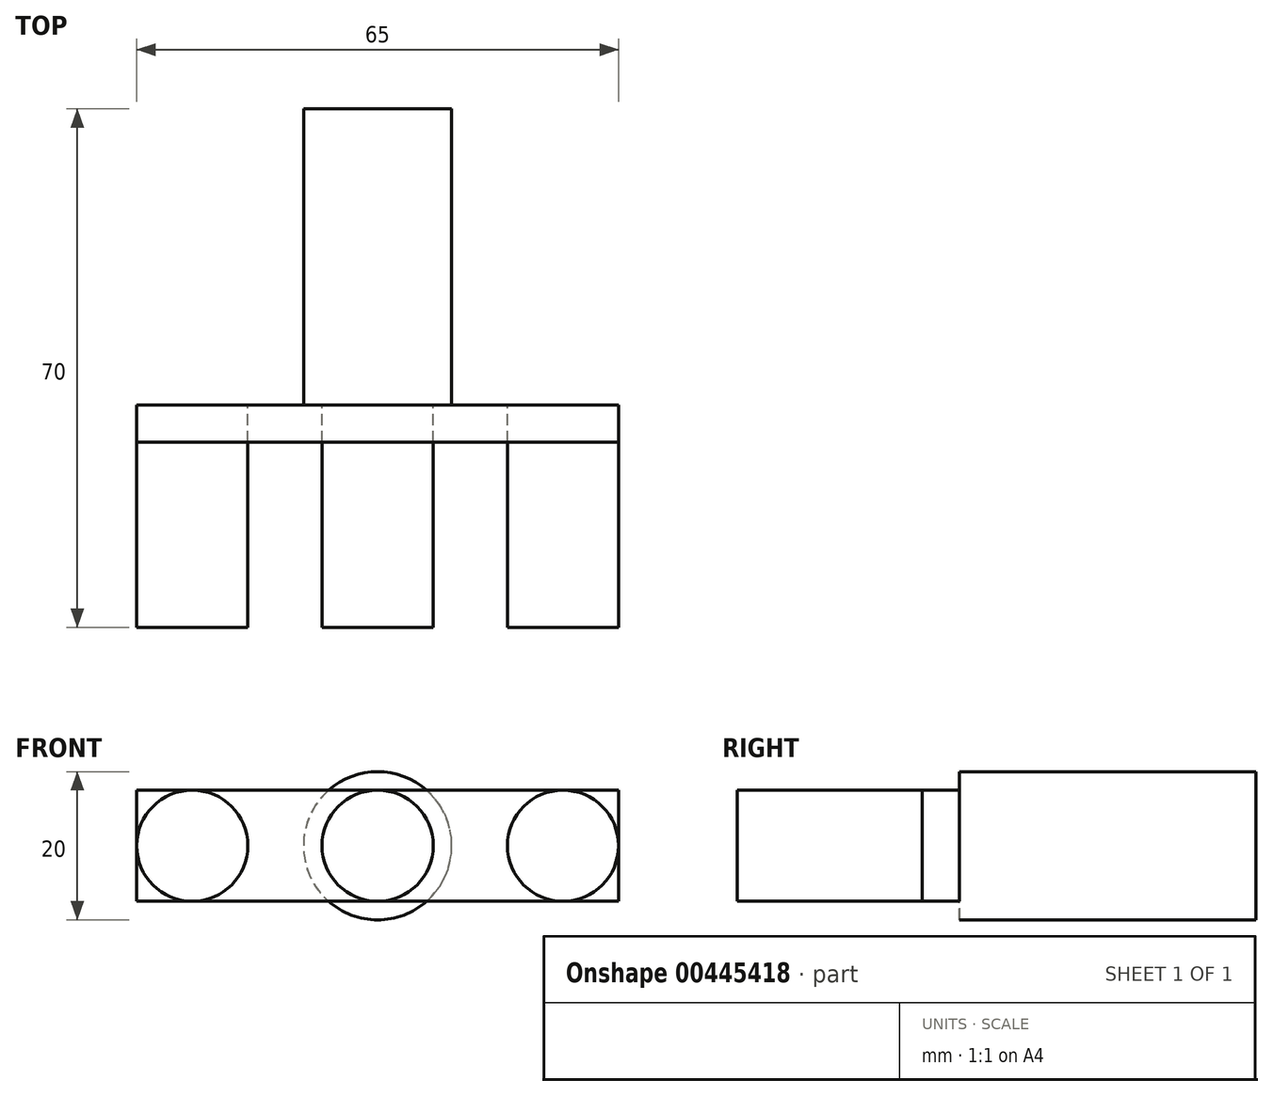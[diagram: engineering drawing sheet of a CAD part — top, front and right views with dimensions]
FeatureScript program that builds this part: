
annotation { "Feature Type Name" : "Feature", "Feature Type Description" : "" }
export const myFeature = defineFeature(function(context is Context, id is Id, definition is map)
    precondition{}
    {
        {
            var Q0;
            Q0=qCreatedBy(makeId("Front.planeOp"),FACE);
            var sketch = newSketch(context, id + "F0", { "sketchPlane" : qUnion([Q0])});
            skLineSegment(sketch, "E0.bottom", {"start": v(32.5, -7.5) * mm, "end": v(-32.5, -7.5) * mm});
            skLineSegment(sketch, "E0.top", {"start": v(32.5, 7.5) * mm, "end": v(-32.5, 7.5) * mm});
            skLineSegment(sketch, "E0.left", {"start": v(32.5, -7.5) * mm, "end": v(32.5, 7.5) * mm});
            skLineSegment(sketch, "E0.right", {"start": v(-32.5, -7.5) * mm, "end": v(-32.5, 7.5) * mm});
            skPoint(sketch, "E0.middle", {"position": v(0, 0) * mm});
            skCircle(sketch, "E1", {"center": v(0, 0) * mm, "radius": 7.5 * mm});
            skCircle(sketch, "E2", {"center": v(25, 0) * mm, "radius": 7.5 * mm});
            skCircle(sketch, "E3", {"center": v(-25, 0) * mm, "radius": 7.5 * mm});
            skSolve(sketch);
        }
        {
            var Q0;
            {var subQ0=sQuery(id+"F0.wireOp",EDGE,"E0.left");var subQ1=sQuery(id+"F0.wireOp",EDGE,"E0.bottom");var subQ2=makeQuery(id+"F0.imprint","INTERSECT",VERTEX,{"derivedFrom":[subQ1,subQ0]});Q0=makeQuery(id+"F0.imprint","IMPRINT",FACE,{"disambiguationData":[TD([[makeQuery(id+"F0.imprint","IMPRINT",EDGE,{"disambiguationData":[TD([[subQ2,-1.0]])],"derivedFrom":subQ1}),-1.0]])]});}
            var Q1;
            {var subQ0=sQuery(id+"F0.wireOp",EDGE,"E0.right");var subQ1=sQuery(id+"F0.wireOp",EDGE,"E0.bottom");var subQ2=makeQuery(id+"F0.imprint","INTERSECT",VERTEX,{"derivedFrom":[subQ1,subQ0]});Q1=makeQuery(id+"F0.imprint","IMPRINT",FACE,{"disambiguationData":[TD([[makeQuery(id+"F0.imprint","IMPRINT",EDGE,{"disambiguationData":[TD([[subQ2,1.0]])],"derivedFrom":subQ1}),-1.0]])]});}
            var Q2;
            {var subQ0=sQuery(id+"F0.wireOp",EDGE,"E0.left");var subQ1=sQuery(id+"F0.wireOp",EDGE,"E0.top");var subQ2=makeQuery(id+"F0.imprint","INTERSECT",VERTEX,{"derivedFrom":[subQ1,subQ0]});Q2=makeQuery(id+"F0.imprint","IMPRINT",FACE,{"disambiguationData":[TD([[makeQuery(id+"F0.imprint","IMPRINT",EDGE,{"disambiguationData":[TD([[subQ2,-1.0]])],"derivedFrom":subQ1}),1.0]])]});}
            var Q3;
            {var subQ0=sQuery(id+"F0.wireOp",EDGE,"E0.right");var subQ1=sQuery(id+"F0.wireOp",EDGE,"E0.top");var subQ2=makeQuery(id+"F0.imprint","INTERSECT",VERTEX,{"derivedFrom":[subQ1,subQ0]});Q3=makeQuery(id+"F0.imprint","IMPRINT",FACE,{"disambiguationData":[TD([[makeQuery(id+"F0.imprint","IMPRINT",EDGE,{"disambiguationData":[TD([[subQ2,1.0]])],"derivedFrom":subQ1}),1.0]])]});}
            var Q4;
            {var subQ0=sQuery(id+"F0.wireOp",EDGE,"E1");var subQ1=sQuery(id+"F0.wireOp",EDGE,"E0.bottom");var subQ2=makeQuery(id+"F0.imprint","INTERSECT",VERTEX,{"derivedFrom":[subQ1,subQ0]});Q4=makeQuery(id+"F0.imprint","IMPRINT",FACE,{"disambiguationData":[TD([[makeQuery(id+"F0.imprint","IMPRINT",EDGE,{"disambiguationData":[TD([[subQ2,-1.0]])],"derivedFrom":subQ1}),-1.0]])]});}
            var Q5;
            {var subQ0=sQuery(id+"F0.wireOp",EDGE,"E3");var subQ1=makeQuery(id+"F0.imprint","INTERSECT",VERTEX,{"derivedFrom":[sQuery(id+"F0.wireOp",EDGE,"E0.top"),subQ0]});Q5=makeQuery(id+"F0.imprint","IMPRINT",FACE,{"disambiguationData":[TD([[makeQuery(id+"F0.imprint","IMPRINT",EDGE,{"disambiguationData":[TD([[subQ1,-1.0]])],"derivedFrom":subQ0}),1.0]])]});}
            var Q6;
            {var subQ0=sQuery(id+"F0.wireOp",EDGE,"E1");var subQ1=makeQuery(id+"F0.imprint","INTERSECT",VERTEX,{"derivedFrom":[sQuery(id+"F0.wireOp",EDGE,"E0.bottom"),subQ0]});Q6=makeQuery(id+"F0.imprint","IMPRINT",FACE,{"disambiguationData":[TD([[makeQuery(id+"F0.imprint","IMPRINT",EDGE,{"disambiguationData":[TD([[subQ1,1.0]])],"derivedFrom":subQ0}),1.0]])]});}
            var Q7;
            {var subQ0=sQuery(id+"F0.wireOp",EDGE,"E2");var subQ1=sQuery(id+"F0.wireOp",EDGE,"E0.bottom");var subQ2=makeQuery(id+"F0.imprint","INTERSECT",VERTEX,{"derivedFrom":[subQ1,subQ0]});Q7=makeQuery(id+"F0.imprint","IMPRINT",FACE,{"disambiguationData":[TD([[makeQuery(id+"F0.imprint","IMPRINT",EDGE,{"disambiguationData":[TD([[subQ2,-1.0]])],"derivedFrom":subQ1}),-1.0]])]});}
            var Q8;
            {var subQ0=sQuery(id+"F0.wireOp",EDGE,"E2");var subQ1=makeQuery(id+"F0.imprint","INTERSECT",VERTEX,{"derivedFrom":[sQuery(id+"F0.wireOp",EDGE,"E0.top"),subQ0]});Q8=makeQuery(id+"F0.imprint","IMPRINT",FACE,{"disambiguationData":[TD([[makeQuery(id+"F0.imprint","IMPRINT",EDGE,{"disambiguationData":[TD([[subQ1,1.0]])],"derivedFrom":subQ0}),1.0]])]});}
            extrude(context, id + "F1", {"entities" : qUnion([Q0, Q1, Q2, Q3, Q4, Q5, Q6, Q7, Q8]), "depth" : 5 * mm});
        }
        {
            var Q0;
            {var subQ0=sQuery(id+"F0.wireOp",EDGE,"E3");var subQ1=makeQuery(id+"F0.imprint","INTERSECT",VERTEX,{"derivedFrom":[sQuery(id+"F0.wireOp",EDGE,"E0.top"),subQ0]});Q0=makeQuery(id+"F0.imprint","IMPRINT",FACE,{"disambiguationData":[TD([[makeQuery(id+"F0.imprint","IMPRINT",EDGE,{"disambiguationData":[TD([[subQ1,-1.0]])],"derivedFrom":subQ0}),1.0]])]});}
            var Q1;
            {var subQ0=sQuery(id+"F0.wireOp",EDGE,"E2");var subQ1=makeQuery(id+"F0.imprint","INTERSECT",VERTEX,{"derivedFrom":[sQuery(id+"F0.wireOp",EDGE,"E0.top"),subQ0]});Q1=makeQuery(id+"F0.imprint","IMPRINT",FACE,{"disambiguationData":[TD([[makeQuery(id+"F0.imprint","IMPRINT",EDGE,{"disambiguationData":[TD([[subQ1,1.0]])],"derivedFrom":subQ0}),1.0]])]});}
            var Q2;
            {var subQ0=sQuery(id+"F0.wireOp",EDGE,"E1");var subQ1=makeQuery(id+"F0.imprint","INTERSECT",VERTEX,{"derivedFrom":[sQuery(id+"F0.wireOp",EDGE,"E0.bottom"),subQ0]});Q2=makeQuery(id+"F0.imprint","IMPRINT",FACE,{"disambiguationData":[TD([[makeQuery(id+"F0.imprint","IMPRINT",EDGE,{"disambiguationData":[TD([[subQ1,1.0]])],"derivedFrom":subQ0}),1.0]])]});}
            extrude(context, id + "F2", {"entities" : qUnion([Q0, Q1, Q2]), "depth" : 30 * mm});
        }
        {
            var Q0;
            Q0=qCreatedBy(makeId("Front.planeOp"),FACE);
            var sketch = newSketch(context, id + "F3", { "sketchPlane" : qUnion([Q0])});
            skCircle(sketch, "E4", {"center": v(0, 0) * mm, "radius": 10 * mm});
            skSolve(sketch);
        }
        {
            var Q0;
            Q0 = qSketchRegion(id + "F3", true);
            extrude(context, id + "F4", {"entities" : qUnion([Q0]), "oppositeDirection" : true, "depth" : 40 * mm});
        }
    });
